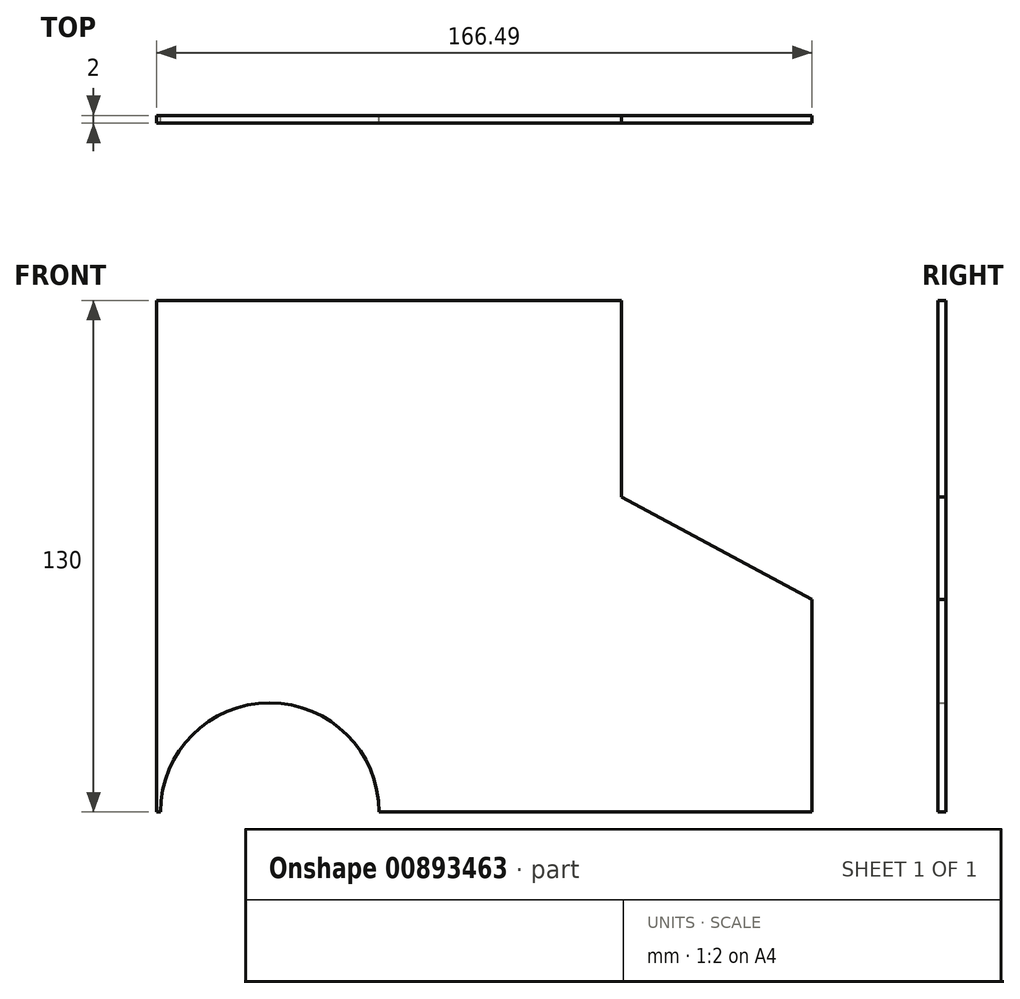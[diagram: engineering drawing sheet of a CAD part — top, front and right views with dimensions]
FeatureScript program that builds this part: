
annotation { "Feature Type Name" : "Feature", "Feature Type Description" : "" }
export const myFeature = defineFeature(function(context is Context, id is Id, definition is map)
    precondition{}
    {
        {
            var Q0;
            Q0=qCreatedBy(makeId("Front.planeOp"),FACE);
            var sketch = newSketch(context, id + "F0", { "sketchPlane" : qUnion([Q0])});
            skLineSegment(sketch, "E0.bottom", {"start": v(0, 0) * mm, "end": v(1, 0) * mm});
            skLineSegment(sketch, "E0.top", {"start": v(0, 130) * mm, "end": v(130, 130) * mm});
            skLineSegment(sketch, "E0.left", {"start": v(0, 0) * mm, "end": v(0, 130) * mm});
            skLineSegment(sketch, "E0.right", {"start": v(166.5, 0) * mm, "end": v(166.5, 54.06) * mm});
            skLineSegment(sketch, "E1", {"start": v(118.04, 80.09) * mm, "end": v(166.5, 54.06) * mm});
            skArc(sketch, "E2", {"start": v(56.5, 0) * mm, "mid": v(28.75, 27.75) * mm, "end": v(1, 0) * mm});
            skLineSegment(sketch, "E3.trimOffspring", {"start": v(56.5, 0) * mm, "end": v(166.5, 0) * mm});
            skLineSegment(sketch, "E4", {"start": v(118.04, 80.09) * mm, "end": v(118.04, 130) * mm});
            skSolve(sketch);
        }
        {
            var Q0;
            Q0 = qSketchRegion(id + "F0", true);
            extrude(context, id + "F1", {"entities" : qUnion([Q0]), "depth" : 2 * mm, "offsetDistance" : 25.4 * mm});
        }
    });
